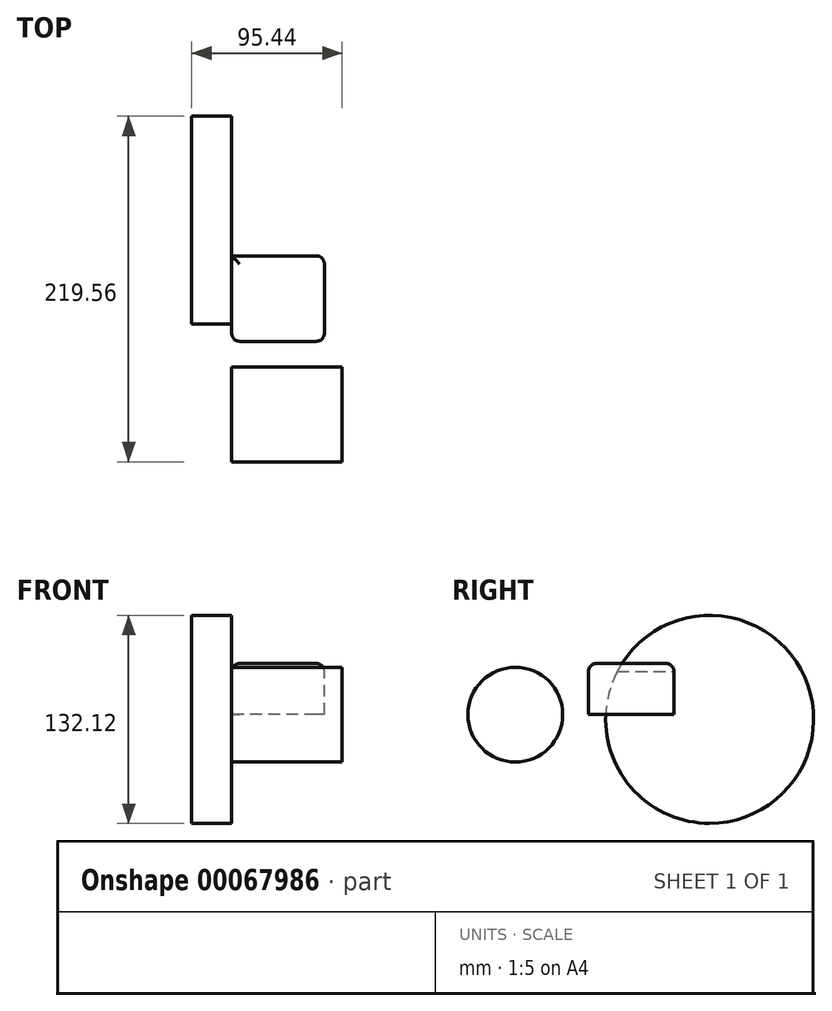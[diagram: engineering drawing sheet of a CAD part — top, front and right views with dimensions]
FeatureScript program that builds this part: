
annotation { "Feature Type Name" : "Feature", "Feature Type Description" : "" }
export const myFeature = defineFeature(function(context is Context, id is Id, definition is map)
    precondition{}
    {
        {
            var Q0;
            Q0=qCreatedBy(makeId("Right.planeOp"),FACE);
            var sketch = newSketch(context, id + "F0", { "sketchPlane" : qUnion([Q0])});
            skLineSegment(sketch, "E0.bottom", {"start": v(0, 0) * mm, "end": v(54.22, 0) * mm});
            skLineSegment(sketch, "E0.top", {"start": v(0, 32.52) * mm, "end": v(54.22, 32.52) * mm});
            skLineSegment(sketch, "E0.left", {"start": v(0, 0) * mm, "end": v(0, 32.52) * mm});
            skLineSegment(sketch, "E0.right", {"start": v(54.22, 0) * mm, "end": v(54.22, 32.52) * mm});
            skSolve(sketch);
        }
        {
            var Q0;
            Q0 = qSketchRegion(id + "F0", true);
            extrude(context, id + "F1", {"entities" : qUnion([Q0]), "depth" : 58.82 * mm});
        }
        {
            var Q0;
            Q0=makeQuery(id+"F1.opExtrude","SWEPT_EDGE",EDGE,{"disambiguationData":[OSD([sQuery(id+"F0.wireOp",EDGE,"E0.top"),sQuery(id+"F0.wireOp",EDGE,"E0.left")])]});
            var Q1;
            Q1=makeQuery(id+"F1.opExtrude","CAP_EDGE",EDGE,{"disambiguationData":[OSD([sQuery(id+"F0.wireOp",EDGE,"E0.top")])],"isStart":false});
            var Q2;
            Q2=makeQuery(id+"F1.opExtrude","SWEPT_EDGE",EDGE,{"disambiguationData":[OSD([sQuery(id+"F0.wireOp",EDGE,"E0.top"),sQuery(id+"F0.wireOp",EDGE,"E0.right")])]});
            var Q3;
            Q3=makeQuery(id+"F1.opExtrude","CAP_EDGE",EDGE,{"disambiguationData":[OSD([sQuery(id+"F0.wireOp",EDGE,"E0.top")])],"isStart":true});
            var Q4;
            Q4=makeQuery(id+"F1.opExtrude","CAP_EDGE",EDGE,{"disambiguationData":[OSD([sQuery(id+"F0.wireOp",EDGE,"E0.left")])],"isStart":false});
            var Q5;
            Q5=makeQuery(id+"F1.opExtrude","CAP_EDGE",EDGE,{"disambiguationData":[OSD([sQuery(id+"F0.wireOp",EDGE,"E0.right")])],"isStart":false});
            var Q6;
            Q6=makeQuery(id+"F1.opExtrude","CAP_EDGE",EDGE,{"disambiguationData":[OSD([sQuery(id+"F0.wireOp",EDGE,"E0.left")])],"isStart":true});
            fillet(context, id + "F2", {"entities" : qUnion([Q0, Q1, Q2, Q3, Q4, Q5, Q6]), "radius" : 5.08 * mm, "tangentPropagation" : true, "allowEdgeOverflow" : false});
        }
        {
            var Q0;
            Q0=qCreatedBy(makeId("Right.planeOp"),FACE);
            var sketch = newSketch(context, id + "F3", { "sketchPlane" : qUnion([Q0])});
            skCircle(sketch, "E1", {"center": v(-46.48, 0) * mm, "radius": 30.08 * mm});
            skSolve(sketch);
        }
        {
            var Q0;
            Q0=makeQuery(id+"F3.imprint","IMPRINT",FACE,{"disambiguationData":[TD([[makeQuery(id+"F3.imprint","IMPRINT",EDGE,{"derivedFrom":sQuery(id+"F3.wireOp",EDGE,"E1")}),1.0]])]});
            extrude(context, id + "F4", {"entities" : qUnion([Q0]), "depth" : 70.04 * mm});
        }
        {
            var Q0;
            Q0=qCreatedBy(makeId("Right.planeOp"),FACE);
            var sketch = newSketch(context, id + "F5", { "sketchPlane" : qUnion([Q0])});
            skCircle(sketch, "E2", {"center": v(76.95, -3) * mm, "radius": 66.06 * mm});
            skSolve(sketch);
        }
        {
            var Q0;
            Q0 = qSketchRegion(id + "F5", true);
            extrude(context, id + "F6", {"entities" : qUnion([Q0]), "operationType" : NewBodyOperationType.ADD, "oppositeDirection" : true, "depth" : 25.4 * mm});
        }
    });
